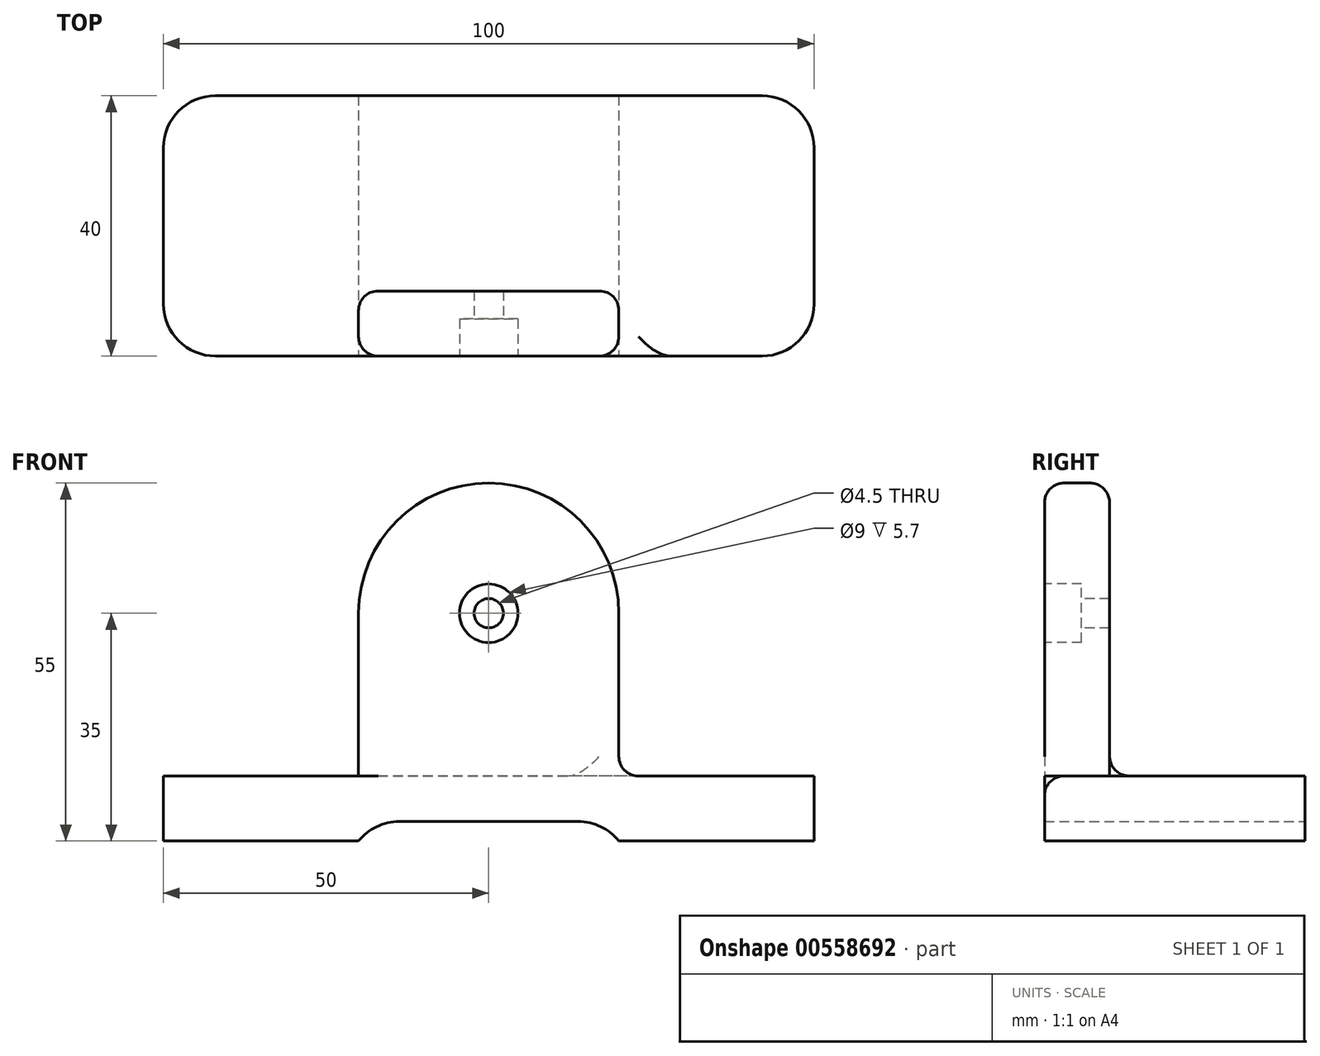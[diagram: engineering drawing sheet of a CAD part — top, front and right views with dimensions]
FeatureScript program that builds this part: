
annotation { "Feature Type Name" : "Feature", "Feature Type Description" : "" }
export const myFeature = defineFeature(function(context is Context, id is Id, definition is map)
    precondition{}
    {
        {
            var Q0;
            Q0=qCreatedBy(makeId("Top.planeOp"),FACE);
            var sketch = newSketch(context, id + "F0", { "sketchPlane" : qUnion([Q0])});
            skLineSegment(sketch, "E0.bottom", {"start": v(0, 0) * mm, "end": v(-100, 0) * mm});
            skLineSegment(sketch, "E0.top", {"start": v(0, 40) * mm, "end": v(-100, 40) * mm});
            skLineSegment(sketch, "E0.left", {"start": v(0, 0) * mm, "end": v(0, 40) * mm});
            skLineSegment(sketch, "E0.right", {"start": v(-100, 0) * mm, "end": v(-100, 40) * mm});
            skSolve(sketch);
        }
        {
            var Q0;
            Q0=makeQuery(id+"F0.imprint","IMPRINT",FACE,{"disambiguationData":[TD([[makeQuery(id+"F0.imprint","IMPRINT",EDGE,{"derivedFrom":sQuery(id+"F0.wireOp",EDGE,"E0.bottom")}),-1.0]])]});
            extrude(context, id + "F1", {"entities" : qUnion([Q0]), "depth" : 10 * mm});
        }
        {
            var Q0;
            Q0=qCreatedBy(makeId("Front.planeOp"),FACE);
            var sketch = newSketch(context, id + "F2", { "sketchPlane" : qUnion([Q0])});
            skLineSegment(sketch, "E1", {"start": v(-70, 0) * mm, "end": v(-70, 35) * mm});
            skArc(sketch, "E2", {"start": v(-70, 35) * mm, "mid": v(-50, 55) * mm, "end": v(-30, 35) * mm});
            skLineSegment(sketch, "E3", {"start": v(-30, 35) * mm, "end": v(-30, 0) * mm});
            skLineSegment(sketch, "E4", {"start": v(-30, 0) * mm, "end": v(-70, 0) * mm});
            skLineSegment(sketch, "E5", {"start": v(-70, 0) * mm, "end": v(-30, 0) * mm});
            skLineSegment(sketch, "E6", {"start": v(-50, -0.11) * mm, "end": v(-70, 0) * mm});
            skSolve(sketch);
        }
        {
            var Q0;
            Q0=qSketchRegion(id+"F2",true);
            extrude(context, id + "F3", {"entities" : qUnion([Q0]), "operationType" : NewBodyOperationType.ADD, "oppositeDirection" : true, "depth" : 10 * mm});
        }
        {
            var Q0;
            Q0=makeQuery(id+"F3.boolean.opBoolean","MERGE",FACE,{"derivedFrom":[makeQuery(id+"F1.opExtrude","SWEPT_FACE",FACE,{"disambiguationData":[OSD([sQuery(id+"F0.wireOp",EDGE,"E0.bottom")])]}),makeQuery(id+"F3.opExtrude","CAP_FACE",FACE,{"disambiguationData":[OSD([sQuery(id+"F2.wireOp",EDGE,"E1"),sQuery(id+"F2.wireOp",EDGE,"E2"),sQuery(id+"F2.wireOp",EDGE,"E3"),sQuery(id+"F2.wireOp",EDGE,"E5")])],"isStart":true})]});
            var sketch = newSketch(context, id + "F4", { "sketchPlane" : qUnion([Q0])});
            skLineSegment(sketch, "E7.bottom", {"start": v(-70, 0) * mm, "end": v(-30, 0) * mm});
            skLineSegment(sketch, "E7.top", {"start": v(-70, 3) * mm, "end": v(-30, 3) * mm});
            skLineSegment(sketch, "E7.left", {"start": v(-70, 0) * mm, "end": v(-70, 3) * mm});
            skLineSegment(sketch, "E7.right", {"start": v(-30, 0) * mm, "end": v(-30, 3) * mm});
            skSolve(sketch);
        }
        {
            var Q0;
            Q0=qSketchRegion(id+"F4",true);
            extrude(context, id + "F5", {"entities" : qUnion([Q0]), "operationType" : NewBodyOperationType.REMOVE, "endBound" : BoundingType.THROUGH_ALL, "oppositeDirection" : true, "depth" : 25 * mm});
        }
        {
            var Q0;
            Q0=makeQuery(id+"F3.boolean.opBoolean","MERGE",FACE,{"derivedFrom":[makeQuery(id+"F1.opExtrude","SWEPT_FACE",FACE,{"disambiguationData":[OSD([sQuery(id+"F0.wireOp",EDGE,"E0.bottom")])]}),makeQuery(id+"F3.opExtrude","CAP_FACE",FACE,{"disambiguationData":[OSD([sQuery(id+"F2.wireOp",EDGE,"E1"),sQuery(id+"F2.wireOp",EDGE,"E2"),sQuery(id+"F2.wireOp",EDGE,"E3"),sQuery(id+"F2.wireOp",EDGE,"E5")])],"isStart":true})]});
            var sketch = newSketch(context, id + "F6", { "sketchPlane" : qUnion([Q0])});
            skCircle(sketch, "E8", {"center": v(-50, 35) * mm, "radius": 2.25 * mm});
            skSolve(sketch);
        }
        {
            var Q0;
            Q0=qSketchRegion(id+"F6",true);
            extrude(context, id + "F7", {"entities" : qUnion([Q0]), "operationType" : NewBodyOperationType.REMOVE, "depth" : 5.7 * mm});
        }
        {
            var Q0;
            Q0=makeQuery(id+"F3.boolean.opBoolean","MERGE",FACE,{"derivedFrom":[makeQuery(id+"F1.opExtrude","SWEPT_FACE",FACE,{"disambiguationData":[OSD([sQuery(id+"F0.wireOp",EDGE,"E0.bottom")])]}),makeQuery(id+"F3.opExtrude","CAP_FACE",FACE,{"disambiguationData":[OSD([sQuery(id+"F2.wireOp",EDGE,"E1"),sQuery(id+"F2.wireOp",EDGE,"E2"),sQuery(id+"F2.wireOp",EDGE,"E3"),sQuery(id+"F2.wireOp",EDGE,"E5")])],"isStart":true})]});
            var sketch = newSketch(context, id + "F8", { "sketchPlane" : qUnion([Q0])});
            skCircle(sketch, "E9", {"center": v(-50, 35) * mm, "radius": 2.25 * mm});
            skSolve(sketch);
        }
        {
            var Q0;
            Q0=qSketchRegion(id+"F8",true);
            extrude(context, id + "F9", {"entities" : qUnion([Q0]), "operationType" : NewBodyOperationType.REMOVE, "endBound" : BoundingType.THROUGH_ALL, "oppositeDirection" : true, "depth" : 5.7 * mm});
        }
        {
            var Q0;
            Q0=makeQuery(id+"F3.boolean.opBoolean","MERGE",FACE,{"derivedFrom":[makeQuery(id+"F1.opExtrude","SWEPT_FACE",FACE,{"disambiguationData":[OSD([sQuery(id+"F0.wireOp",EDGE,"E0.bottom")])]}),makeQuery(id+"F3.opExtrude","CAP_FACE",FACE,{"disambiguationData":[OSD([sQuery(id+"F2.wireOp",EDGE,"E1"),sQuery(id+"F2.wireOp",EDGE,"E2"),sQuery(id+"F2.wireOp",EDGE,"E3"),sQuery(id+"F2.wireOp",EDGE,"E5")])],"isStart":true})]});
            var sketch = newSketch(context, id + "F10", { "sketchPlane" : qUnion([Q0])});
            skCircle(sketch, "E10", {"center": v(-50, 35) * mm, "radius": 4.5 * mm});
            skSolve(sketch);
        }
        {
            var Q0;
            Q0=qSketchRegion(id+"F10",true);
            extrude(context, id + "F11", {"entities" : qUnion([Q0]), "operationType" : NewBodyOperationType.REMOVE, "oppositeDirection" : true, "depth" : 5.7 * mm});
        }
        {
            var Q0;
            Q0=makeQuery(id+"F5.boolean.opBoolean","COPY",EDGE,{"derivedFrom":makeQuery(id+"F5.opExtrude","SWEPT_EDGE",EDGE,{"disambiguationData":[OSD([sQuery(id+"F4.wireOp",EDGE,"E7.top"),sQuery(id+"F4.wireOp",EDGE,"E7.left")])]})});
            var Q1;
            Q1=makeQuery(id+"F5.boolean.opBoolean","COPY",EDGE,{"derivedFrom":makeQuery(id+"F5.opExtrude","SWEPT_EDGE",EDGE,{"disambiguationData":[OSD([sQuery(id+"F4.wireOp",EDGE,"E7.top"),sQuery(id+"F4.wireOp",EDGE,"E7.right")])]})});
            var Q2;
            Q2=makeQuery(id+"F1.opExtrude","SWEPT_EDGE",EDGE,{"disambiguationData":[OSD([sQuery(id+"F0.wireOp",EDGE,"E0.bottom"),sQuery(id+"F0.wireOp",EDGE,"E0.left")])]});
            var Q3;
            Q3=makeQuery(id+"F1.opExtrude","SWEPT_EDGE",EDGE,{"disambiguationData":[OSD([sQuery(id+"F0.wireOp",EDGE,"E0.top"),sQuery(id+"F0.wireOp",EDGE,"E0.left")])]});
            var Q4;
            Q4=makeQuery(id+"F1.opExtrude","SWEPT_EDGE",EDGE,{"disambiguationData":[OSD([sQuery(id+"F0.wireOp",EDGE,"E0.bottom"),sQuery(id+"F0.wireOp",EDGE,"E0.right")])]});
            var Q5;
            Q5=makeQuery(id+"F1.opExtrude","SWEPT_EDGE",EDGE,{"disambiguationData":[OSD([sQuery(id+"F0.wireOp",EDGE,"E0.top"),sQuery(id+"F0.wireOp",EDGE,"E0.right")])]});
            fillet(context, id + "F12", {"entities" : qUnion([Q0, Q1, Q2, Q3, Q4, Q5]), "radius" : 8 * mm, "tangentPropagation" : true, "allowEdgeOverflow" : false});
        }
        {
            var Q0;
            Q0=makeQuery(id+"F3.opExtrude","SWEPT_FACE",FACE,{"disambiguationData":[OSD([sQuery(id+"F2.wireOp",EDGE,"E2")])]});
            var Q1;
            Q1=makeQuery(id+"F3.boolean.opBoolean","INTERSECT",EDGE,{"derivedFrom":[makeQuery(id+"F1.opExtrude","CAP_FACE",FACE,{"disambiguationData":[OSD([sQuery(id+"F0.wireOp",EDGE,"E0.bottom"),sQuery(id+"F0.wireOp",EDGE,"E0.top"),sQuery(id+"F0.wireOp",EDGE,"E0.left"),sQuery(id+"F0.wireOp",EDGE,"E0.right")])],"isStart":false}),makeQuery(id+"F3.opExtrude","SWEPT_FACE",FACE,{"disambiguationData":[OSD([sQuery(id+"F2.wireOp",EDGE,"E3")])]})]});
            fillet(context, id + "F13", {"entities" : qUnion([Q0, Q1]), "radius" : 3 * mm, "tangentPropagation" : true, "allowEdgeOverflow" : false});
        }
    });
